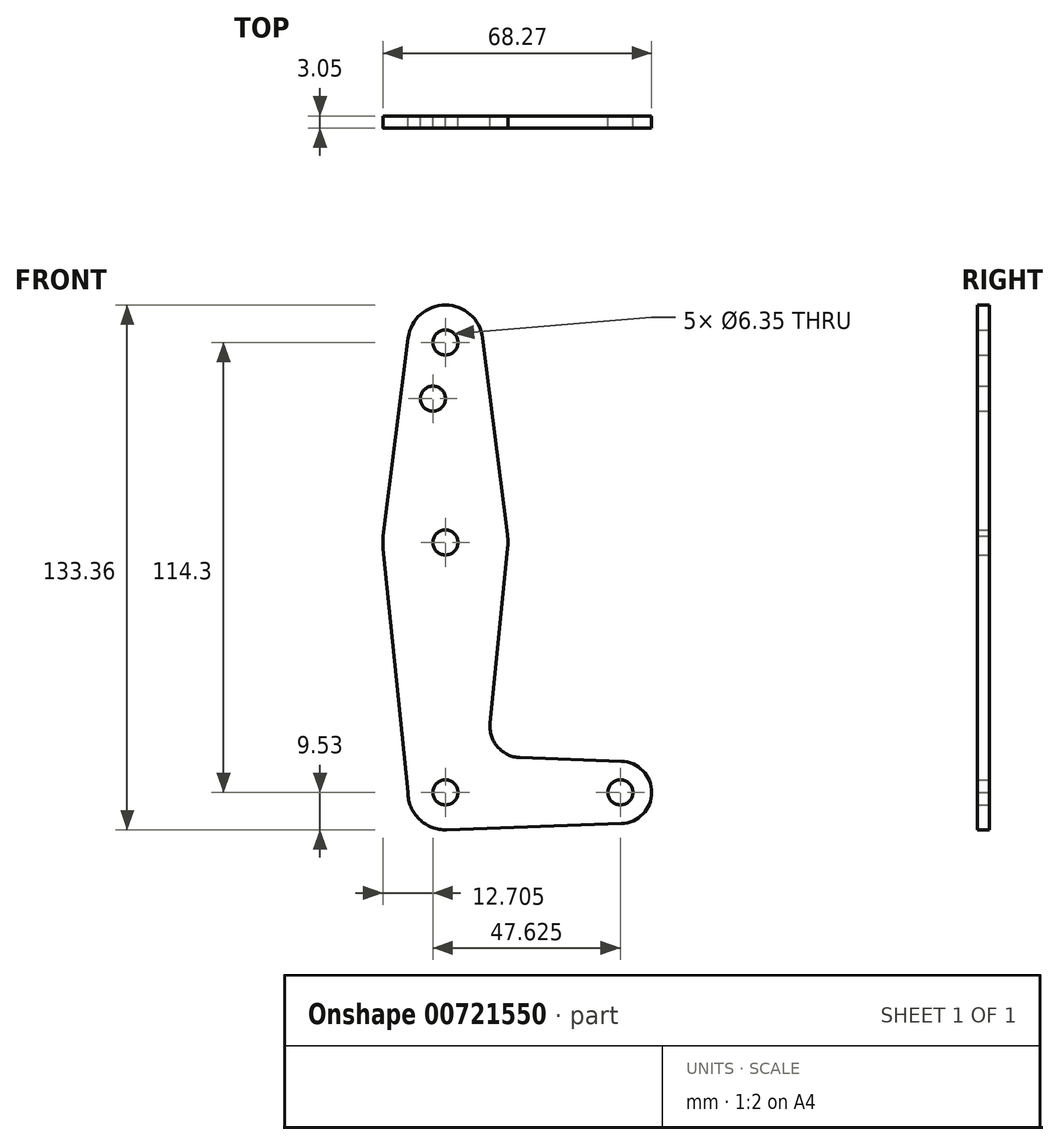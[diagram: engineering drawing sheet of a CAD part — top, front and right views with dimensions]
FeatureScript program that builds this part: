
annotation { "Feature Type Name" : "Feature", "Feature Type Description" : "" }
export const myFeature = defineFeature(function(context is Context, id is Id, definition is map)
    precondition{}
    {
        {
            var Q0;
            Q0=qCreatedBy(makeId("Front.planeOp"),FACE);
            var sketch = newSketch(context, id + "F0", { "sketchPlane" : qUnion([Q0])});
            skLineSegment(sketch, "E0", {"start": v(0, 0) * mm, "end": v(0, 114.3) * mm});
            skLineSegment(sketch, "E1", {"start": v(0, 0) * mm, "end": v(44.45, 0) * mm});
            skCircle(sketch, "E2", {"center": v(0, 114.3) * mm, "radius": 9.53 * mm});
            skCircle(sketch, "E3", {"center": v(0, 0) * mm, "radius": 9.53 * mm});
            skCircle(sketch, "E4", {"center": v(44.45, 0) * mm, "radius": 7.94 * mm});
            skCircle(sketch, "E5", {"center": v(0, 63.5) * mm, "radius": 15.88 * mm});
            skLineSegment(sketch, "E6", {"start": v(9.45, 115.5) * mm, "end": v(15.75, 65.48) * mm});
            skLineSegment(sketch, "E7", {"start": v(15.8, 61.91) * mm, "end": v(11.34, 17.59) * mm});
            skLineSegment(sketch, "E8", {"start": v(18.97, 8.85) * mm, "end": v(44.73, 7.93) * mm});
            skLineSegment(sketch, "E9", {"start": v(44.73, -7.93) * mm, "end": v(0, -9.53) * mm});
            skLineSegment(sketch, "E10", {"start": v(-9.53, 0) * mm, "end": v(-15.8, 61.9) * mm});
            skLineSegment(sketch, "E11", {"start": v(-15.8, 65.1) * mm, "end": v(-9.45, 115.49) * mm});
            skCircle(sketch, "E12", {"center": v(-3.18, 100.03) * mm, "radius": 3.18 * mm});
            skCircle(sketch, "E13", {"center": v(0, 114.3) * mm, "radius": 3.18 * mm});
            skCircle(sketch, "E14", {"center": v(0, 63.5) * mm, "radius": 3.18 * mm});
            skCircle(sketch, "E15", {"center": v(0, 0) * mm, "radius": 3.18 * mm});
            skCircle(sketch, "E16", {"center": v(44.45, 0) * mm, "radius": 3.18 * mm});
            skArc(sketch, "E17.filletArc", {"start": v(11.34, 17.59) * mm, "mid": v(13.26, 11.57) * mm, "end": v(18.97, 8.85) * mm});
            skSolve(sketch);
        }
        {
            var Q0;
            {var subQ0=sQuery(id+"F0.wireOp",EDGE,"E11");var subQ1=sQuery(id+"F0.wireOp",EDGE,"E5");var subQ2=makeQuery(id+"F0.imprint","INTERSECT",VERTEX,{"disambiguationData":[OD(0.0)],"derivedFrom":[subQ1,subQ0]});Q0=makeQuery(id+"F0.imprint","IMPRINT",FACE,{"disambiguationData":[TD([[makeQuery(id+"F0.imprint","IMPRINT",EDGE,{"disambiguationData":[TD([[subQ2,1.0]])],"derivedFrom":subQ1}),1.0]])]});}
            var Q1;
            {var subQ0=sQuery(id+"F0.wireOp",EDGE,"E6");Q1=makeQuery(id+"F0.imprint","IMPRINT",FACE,{"disambiguationData":[TD([[makeQuery(id+"F0.imprint","IMPRINT",EDGE,{"derivedFrom":subQ0}),-1.0]])]});}
            var Q2;
            {var subQ0=sQuery(id+"F0.wireOp",EDGE,"E4");var subQ1=sQuery(id+"F0.wireOp",EDGE,"E1");var subQ2=makeQuery(id+"F0.imprint","INTERSECT",VERTEX,{"derivedFrom":[subQ1,subQ0]});Q2=makeQuery(id+"F0.imprint","IMPRINT",FACE,{"disambiguationData":[TD([[makeQuery(id+"F0.imprint","IMPRINT",EDGE,{"disambiguationData":[TD([[subQ2,1.0]])],"derivedFrom":subQ1}),-1.0]])]});}
            var Q3;
            Q3=makeQuery(id+"F0.imprint","IMPRINT",FACE,{"disambiguationData":[TD([[makeQuery(id+"F0.imprint","IMPRINT",EDGE,{"derivedFrom":sQuery(id+"F0.wireOp",EDGE,"E13")}),-1.0]])]});
            var Q4;
            Q4=makeQuery(id+"F0.imprint","IMPRINT",FACE,{"disambiguationData":[TD([[makeQuery(id+"F0.imprint","IMPRINT",EDGE,{"derivedFrom":sQuery(id+"F0.wireOp",EDGE,"E16")}),-1.0]])]});
            var Q5;
            {var subQ2=sQuery(id+"F0.wireOp",EDGE,"E0");var subQ4=sQuery(id+"F0.wireOp",EDGE,"E15");var subQ9=makeQuery(id+"F0.imprint","INTERSECT",VERTEX,{"derivedFrom":[subQ2,subQ4]});Q5=makeQuery(id+"F0.imprint","IMPRINT",FACE,{"disambiguationData":[TD([[makeQuery(id+"F0.imprint","IMPRINT",EDGE,{"disambiguationData":[TD([[subQ9,-1.0]])],"derivedFrom":subQ2}),1.0]])]});}
            var Q6;
            {var subQ0=sQuery(id+"F0.wireOp",EDGE,"E5");var subQ2=sQuery(id+"F0.wireOp",EDGE,"E0");var subQ3=makeQuery(id+"F0.imprint","INTERSECT",VERTEX,{"disambiguationData":[OD(0.0)],"derivedFrom":[subQ2,subQ0]});Q6=makeQuery(id+"F0.imprint","IMPRINT",FACE,{"disambiguationData":[TD([[makeQuery(id+"F0.imprint","IMPRINT",EDGE,{"disambiguationData":[TD([[subQ3,-1.0]])],"derivedFrom":subQ2}),-1.0]])]});}
            var Q7;
            {var subQ8=sQuery(id+"F0.wireOp",EDGE,"E12");Q7=makeQuery(id+"F0.imprint","IMPRINT",FACE,{"disambiguationData":[TD([[makeQuery(id+"F0.imprint","IMPRINT",EDGE,{"derivedFrom":subQ8}),-1.0]])]});}
            var Q8;
            {var subQ4=sQuery(id+"F0.wireOp",EDGE,"E7");Q8=makeQuery(id+"F0.imprint","IMPRINT",FACE,{"disambiguationData":[TD([[makeQuery(id+"F0.imprint","IMPRINT",EDGE,{"derivedFrom":subQ4}),-1.0]])]});}
            var Q9;
            {var subQ0=sQuery(id+"F0.wireOp",EDGE,"E5");var subQ5=sQuery(id+"F0.wireOp",EDGE,"E0");var subQ9=makeQuery(id+"F0.imprint","INTERSECT",VERTEX,{"disambiguationData":[OD(0.0)],"derivedFrom":[subQ5,subQ0]});Q9=makeQuery(id+"F0.imprint","IMPRINT",FACE,{"disambiguationData":[TD([[makeQuery(id+"F0.imprint","IMPRINT",EDGE,{"disambiguationData":[TD([[subQ9,-1.0]])],"derivedFrom":subQ5}),1.0]])]});}
            var Q10;
            {var subQ5=sQuery(id+"F0.wireOp",EDGE,"E10");Q10=makeQuery(id+"F0.imprint","IMPRINT",FACE,{"disambiguationData":[TD([[makeQuery(id+"F0.imprint","IMPRINT",EDGE,{"derivedFrom":subQ5}),-1.0]])]});}
            var Q11;
            {var subQ0=sQuery(id+"F0.wireOp",EDGE,"E15");var subQ1=sQuery(id+"F0.wireOp",EDGE,"E0");var subQ2=makeQuery(id+"F0.imprint","INTERSECT",VERTEX,{"derivedFrom":[subQ1,subQ0]});Q11=makeQuery(id+"F0.imprint","IMPRINT",FACE,{"disambiguationData":[TD([[makeQuery(id+"F0.imprint","IMPRINT",EDGE,{"disambiguationData":[TD([[subQ2,-1.0]])],"derivedFrom":subQ1}),-1.0]])]});}
            extrude(context, id + "F1", {"entities" : qUnion([Q0, Q1, Q2, Q3, Q4, Q5, Q6, Q7, Q8, Q9, Q10, Q11]), "depth" : 3.05 * mm, "offsetDistance" : 25.4 * mm});
        }
    });
